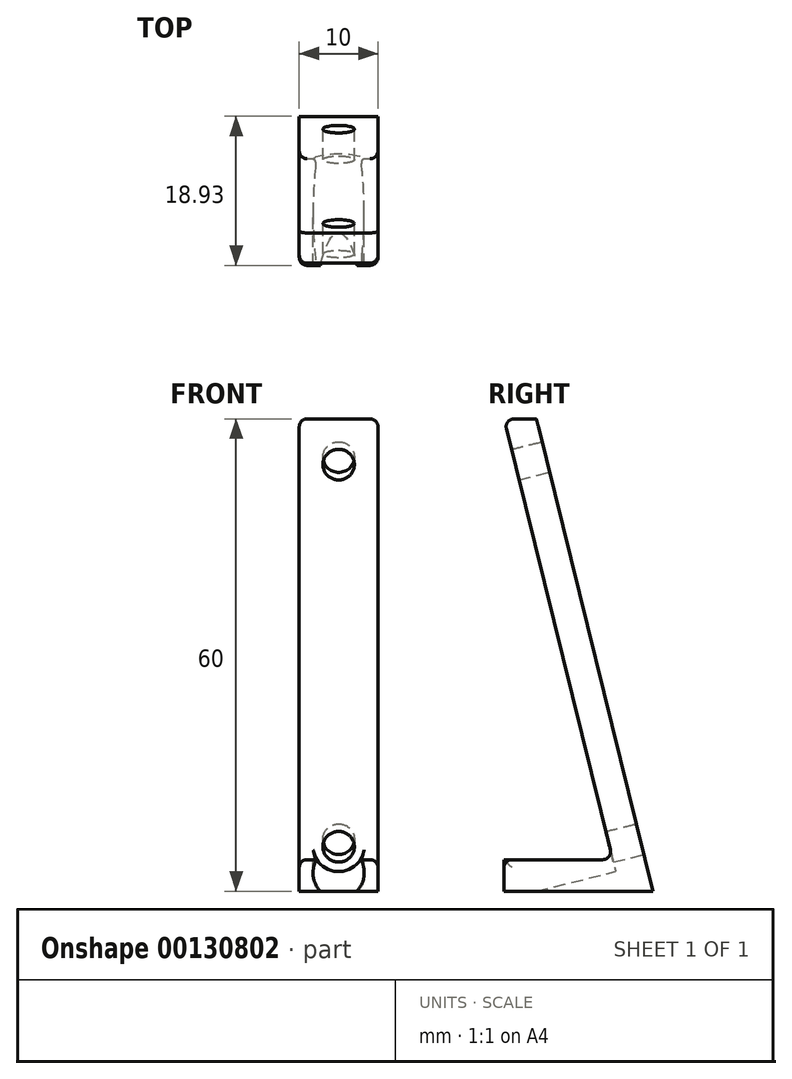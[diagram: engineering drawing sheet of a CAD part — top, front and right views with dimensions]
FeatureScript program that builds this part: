
annotation { "Feature Type Name" : "Feature", "Feature Type Description" : "" }
export const myFeature = defineFeature(function(context is Context, id is Id, definition is map)
    precondition{}
    {
        {
            var Q0;
            Q0=qCreatedBy(makeId("Right.planeOp"),FACE);
            var sketch = newSketch(context, id + "F0", { "sketchPlane" : qUnion([Q0])});
            skLineSegment(sketch, "E0", {"start": v(18.93, 0) * mm, "end": v(0, 0) * mm});
            skLineSegment(sketch, "E1", {"start": v(0, 0) * mm, "end": v(0, 4) * mm});
            skLineSegment(sketch, "E2", {"start": v(0, 4) * mm, "end": v(13.82, 4) * mm});
            skLineSegment(sketch, "E3", {"start": v(13.82, 4) * mm, "end": v(0, 60) * mm});
            skLineSegment(sketch, "E4", {"start": v(0, 60) * mm, "end": v(4.12, 60) * mm});
            skLineSegment(sketch, "E5", {"start": v(4.12, 60) * mm, "end": v(18.93, 0) * mm});
            skSolve(sketch);
        }
        {
            var Q0;
            Q0=makeQuery(id+"F0.imprint","IMPRINT",FACE,{"disambiguationData":[TD([[makeQuery(id+"F0.imprint","IMPRINT",EDGE,{"derivedFrom":sQuery(id+"F0.wireOp",EDGE,"E0")}),-1.0]])]});
            extrude(context, id + "F1", {"entities" : qUnion([Q0]), "endBound" : BoundingType.SYMMETRIC, "depth" : 10 * mm});
        }
        {
            var Q0;
            Q0=makeQuery(id+"F1.opExtrude","SWEPT_FACE",FACE,{"disambiguationData":[OSD([sQuery(id+"F0.wireOp",EDGE,"E5")])]});
            var sketch = newSketch(context, id + "F2", { "sketchPlane" : qUnion([Q0])});
            skCircle(sketch, "E6", {"center": v(0, 2.26) * mm, "radius": 2 * mm});
            skCircle(sketch, "E7", {"center": v(0, 52.26) * mm, "radius": 2 * mm});
            skSolve(sketch);
        }
        {
            var Q0;
            Q0 = qSketchRegion(id + "F2", true);
            extrude(context, id + "F3", {"entities" : qUnion([Q0]), "operationType" : NewBodyOperationType.REMOVE, "endBound" : BoundingType.THROUGH_ALL, "oppositeDirection" : true, "depth" : 25 * mm});
        }
        {
            var Q0;
            Q0=makeQuery(id+"F1.opExtrude","CAP_EDGE",EDGE,{"disambiguationData":[OSD([sQuery(id+"F0.wireOp",EDGE,"E2")])],"isStart":true});
            var Q1;
            Q1=makeQuery(id+"F1.opExtrude","CAP_EDGE",EDGE,{"disambiguationData":[OSD([sQuery(id+"F0.wireOp",EDGE,"E3")])],"isStart":true});
            var Q2;
            Q2=makeQuery(id+"F1.opExtrude","CAP_EDGE",EDGE,{"disambiguationData":[OSD([sQuery(id+"F0.wireOp",EDGE,"E3")])],"isStart":false});
            var Q3;
            Q3=makeQuery(id+"F1.opExtrude","CAP_EDGE",EDGE,{"disambiguationData":[OSD([sQuery(id+"F0.wireOp",EDGE,"E2")])],"isStart":false});
            var Q4;
            {var subQ0=sQuery(id+"F0.wireOp",EDGE,"E2");var subQ1=sQuery(id+"F0.wireOp",EDGE,"E1");Q4=makeQuery(id+"F3.boolean.opBoolean","SPLIT",EDGE,{"disambiguationData":[TD([makeQuery(id+"F1.opExtrude","CAP_FACE",FACE,{"disambiguationData":[OSD([sQuery(id+"F0.wireOp",EDGE,"E0"),subQ1,subQ0,sQuery(id+"F0.wireOp",EDGE,"E3"),sQuery(id+"F0.wireOp",EDGE,"E4"),sQuery(id+"F0.wireOp",EDGE,"E5")])],"isStart":false})])],"derivedFrom":makeQuery(id+"F1.opExtrude","SWEPT_EDGE",EDGE,{"disambiguationData":[OSD([subQ1,subQ0])]})});}
            var Q5;
            Q5=makeQuery(id+"F1.opExtrude","CAP_EDGE",EDGE,{"disambiguationData":[OSD([sQuery(id+"F0.wireOp",EDGE,"E1")])],"isStart":true});
            var Q6;
            Q6=makeQuery(id+"F1.opExtrude","CAP_EDGE",EDGE,{"disambiguationData":[OSD([sQuery(id+"F0.wireOp",EDGE,"E1")])],"isStart":false});
            var Q7;
            Q7=makeQuery(id+"F1.opExtrude","SWEPT_EDGE",EDGE,{"disambiguationData":[OSD([sQuery(id+"F0.wireOp",EDGE,"E3"),sQuery(id+"F0.wireOp",EDGE,"E4")])]});
            var Q8;
            {var subQ0=sQuery(id+"F0.wireOp",EDGE,"E3");var subQ1=sQuery(id+"F0.wireOp",EDGE,"E2");Q8=makeQuery(id+"F3.boolean.opBoolean","SPLIT",EDGE,{"disambiguationData":[TD([makeQuery(id+"F1.opExtrude","CAP_FACE",FACE,{"disambiguationData":[OSD([sQuery(id+"F0.wireOp",EDGE,"E0"),sQuery(id+"F0.wireOp",EDGE,"E1"),subQ1,subQ0,sQuery(id+"F0.wireOp",EDGE,"E4"),sQuery(id+"F0.wireOp",EDGE,"E5")])],"isStart":true})])],"derivedFrom":makeQuery(id+"F1.opExtrude","SWEPT_EDGE",EDGE,{"disambiguationData":[OSD([subQ1,subQ0])]})});}
            var Q9;
            {var subQ0=sQuery(id+"F0.wireOp",EDGE,"E3");var subQ1=sQuery(id+"F0.wireOp",EDGE,"E2");Q9=makeQuery(id+"F3.boolean.opBoolean","SPLIT",EDGE,{"disambiguationData":[TD([makeQuery(id+"F1.opExtrude","CAP_FACE",FACE,{"disambiguationData":[OSD([sQuery(id+"F0.wireOp",EDGE,"E0"),sQuery(id+"F0.wireOp",EDGE,"E1"),subQ1,subQ0,sQuery(id+"F0.wireOp",EDGE,"E4"),sQuery(id+"F0.wireOp",EDGE,"E5")])],"isStart":false})])],"derivedFrom":makeQuery(id+"F1.opExtrude","SWEPT_EDGE",EDGE,{"disambiguationData":[OSD([subQ1,subQ0])]})});}
            fillet(context, id + "F4", {"entities" : qUnion([Q0, Q1, Q2, Q3, Q4, Q5, Q6, Q7, Q8, Q9]), "radius" : 1 * mm, "tangentPropagation" : true, "allowEdgeOverflow" : false});
        }
        {
            var Q0;
            Q0=makeQuery(id+"F1.opExtrude","CAP_EDGE",EDGE,{"disambiguationData":[OSD([sQuery(id+"F0.wireOp",EDGE,"E4")])],"isStart":false});
            var Q1;
            Q1=makeQuery(id+"F1.opExtrude","CAP_EDGE",EDGE,{"disambiguationData":[OSD([sQuery(id+"F0.wireOp",EDGE,"E4")])],"isStart":true});
            fillet(context, id + "F5", {"entities" : qUnion([Q0, Q1]), "radius" : 1 * mm, "tangentPropagation" : true, "allowEdgeOverflow" : false});
        }
        {
            var Q0;
            Q0=makeQuery(id+"F1.opExtrude","SWEPT_FACE",FACE,{"disambiguationData":[OSD([sQuery(id+"F0.wireOp",EDGE,"E3")])]});
            var sketch = newSketch(context, id + "F6", { "sketchPlane" : qUnion([Q0])});
            skCircle(sketch, "E8", {"center": v(0, 2.26) * mm, "radius": 3.25 * mm});
            skSolve(sketch);
        }
        {
            var Q0;
            Q0 = qSketchRegion(id + "F6", true);
            extrude(context, id + "F7", {"entities" : qUnion([Q0]), "operationType" : NewBodyOperationType.REMOVE, "endBound" : BoundingType.THROUGH_ALL, "depth" : 25 * mm});
        }
    });
